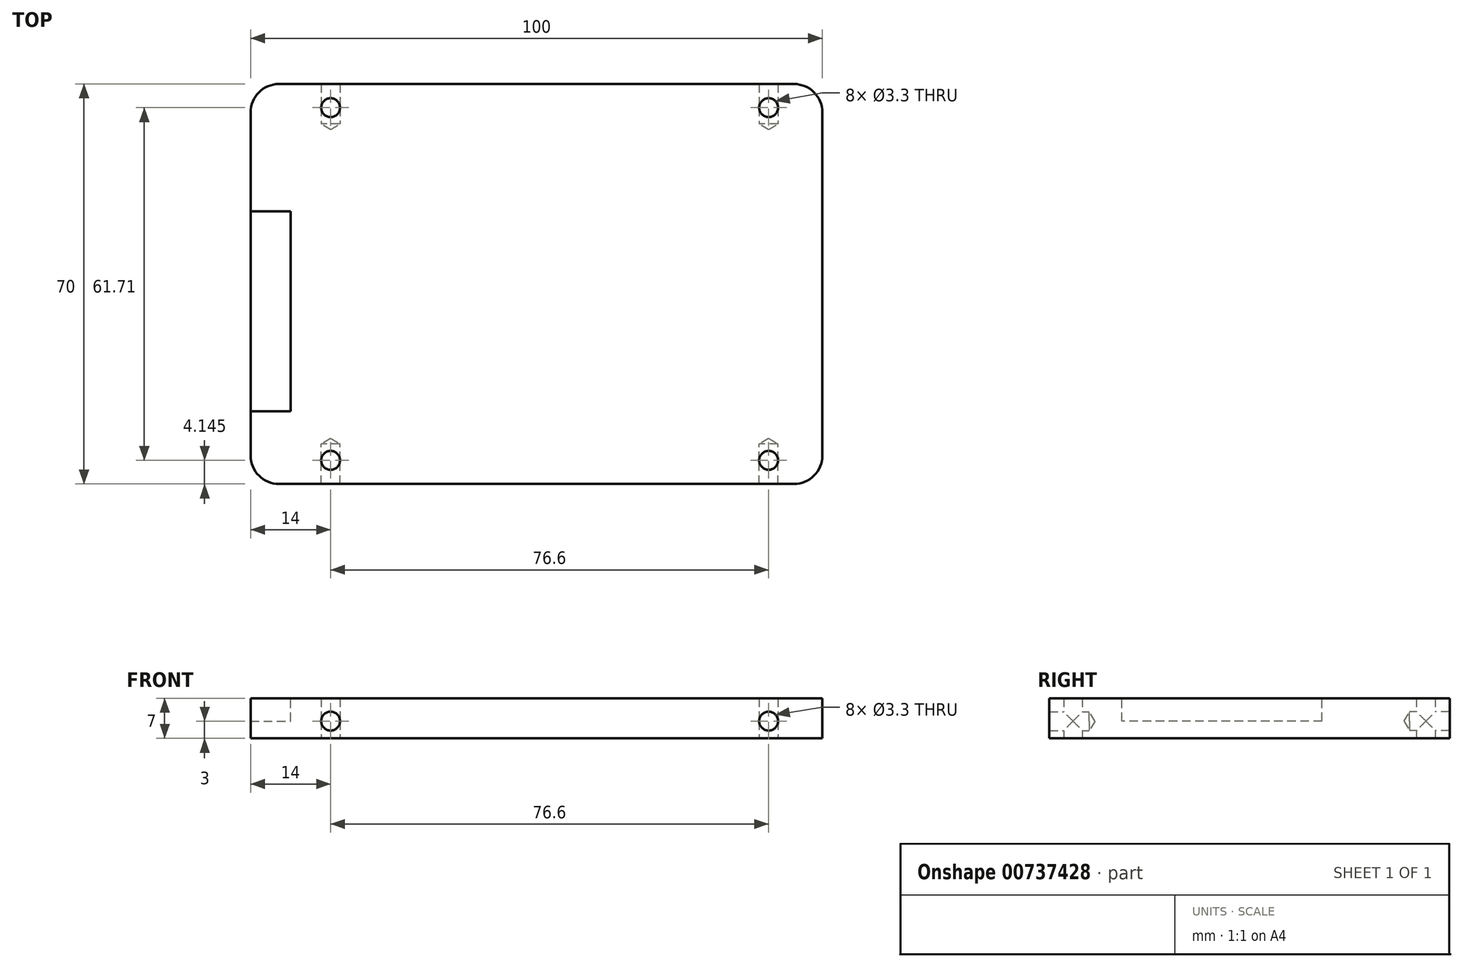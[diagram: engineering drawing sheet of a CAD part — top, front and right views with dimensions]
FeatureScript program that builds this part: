
annotation { "Feature Type Name" : "Feature", "Feature Type Description" : "" }
export const myFeature = defineFeature(function(context is Context, id is Id, definition is map)
    precondition{}
    {
        {
            var Q0;
            Q0=qCreatedBy(makeId("Top.planeOp"),FACE);
            var sketch = newSketch(context, id + "F0", { "sketchPlane" : qUnion([Q0])});
            skLineSegment(sketch, "E0.bottom", {"start": v(-50, 35) * mm, "end": v(50, 35) * mm});
            skLineSegment(sketch, "E0.top", {"start": v(-50, -35) * mm, "end": v(50, -35) * mm});
            skLineSegment(sketch, "E0.left", {"start": v(-50, 35) * mm, "end": v(-50, -35) * mm});
            skLineSegment(sketch, "E0.right", {"start": v(50, 35) * mm, "end": v(50, -35) * mm});
            skSolve(sketch);
        }
        {
            var Q0;
            Q0=makeQuery(id+"F0.imprint","IMPRINT",FACE,{"disambiguationData":[TD([[makeQuery(id+"F0.imprint","IMPRINT",EDGE,{"derivedFrom":sQuery(id+"F0.wireOp",EDGE,"E0.bottom")}),-1.0]])]});
            extrude(context, id + "F1", {"entities" : qUnion([Q0]), "depth" : 7 * mm});
        }
        {
            var Q0;
            Q0=makeQuery(id+"F1.opExtrude","SWEPT_EDGE",EDGE,{"disambiguationData":[OSD([sQuery(id+"F0.wireOp",EDGE,"E0.top"),sQuery(id+"F0.wireOp",EDGE,"E0.left")])]});
            var Q1;
            Q1=makeQuery(id+"F1.opExtrude","SWEPT_EDGE",EDGE,{"disambiguationData":[OSD([sQuery(id+"F0.wireOp",EDGE,"E0.top"),sQuery(id+"F0.wireOp",EDGE,"E0.right")])]});
            var Q2;
            Q2=makeQuery(id+"F1.opExtrude","SWEPT_EDGE",EDGE,{"disambiguationData":[OSD([sQuery(id+"F0.wireOp",EDGE,"E0.bottom"),sQuery(id+"F0.wireOp",EDGE,"E0.left")])]});
            var Q3;
            Q3=makeQuery(id+"F1.opExtrude","SWEPT_EDGE",EDGE,{"disambiguationData":[OSD([sQuery(id+"F0.wireOp",EDGE,"E0.bottom"),sQuery(id+"F0.wireOp",EDGE,"E0.right")])]});
            fillet(context, id + "F2", {"entities" : qUnion([Q0, Q1, Q2, Q3]), "radius" : 5 * mm, "tangentPropagation" : true, "allowEdgeOverflow" : false});
        }
        {
            var Q0;
            Q0=makeQuery(id+"F1.opExtrude","CAP_FACE",FACE,{"disambiguationData":[OSD([sQuery(id+"F0.wireOp",EDGE,"E0.bottom"),sQuery(id+"F0.wireOp",EDGE,"E0.top"),sQuery(id+"F0.wireOp",EDGE,"E0.left"),sQuery(id+"F0.wireOp",EDGE,"E0.right")])],"isStart":false});
            var sketch = newSketch(context, id + "F3", { "sketchPlane" : qUnion([Q0])});
            skPoint(sketch, "E1", {"position": v(-36, 30.86) * mm});
            skPoint(sketch, "E2", {"position": v(40.6, 30.86) * mm});
            skPoint(sketch, "E3", {"position": v(40.6, -30.86) * mm});
            skPoint(sketch, "E4", {"position": v(-36, -30.86) * mm});
            skSolve(sketch);
        }
        {
            var Q0;
            Q0=makeQuery(id+"F1.opExtrude","SWEPT_FACE",FACE,{"disambiguationData":[OSD([sQuery(id+"F0.wireOp",EDGE,"E0.top")])]});
            var sketch = newSketch(context, id + "F4", { "sketchPlane" : qUnion([Q0])});
            skPoint(sketch, "E5", {"position": v(-36, 3) * mm});
            skPoint(sketch, "E6", {"position": v(40.6, 3) * mm});
            skLineSegment(sketch, "E7", {"start": v(-36, 3) * mm, "end": v(-36, 7) * mm, "construction": true});
            skPoint(sketch, "E8.0", {"position": v(-36, 7) * mm});
            skPoint(sketch, "E9.0", {"position": v(40.6, 7) * mm});
            skLineSegment(sketch, "E10", {"start": v(40.6, 3) * mm, "end": v(40.6, 7) * mm, "construction": true});
            skLineSegment(sketch, "E11", {"start": v(-36, 3) * mm, "end": v(40.6, 3) * mm, "construction": true});
            skSolve(sketch);
        }
        {
            var Q0;
            Q0=makeQuery(id+"F1.opExtrude","SWEPT_FACE",FACE,{"disambiguationData":[OSD([sQuery(id+"F0.wireOp",EDGE,"E0.bottom")])]});
            var sketch = newSketch(context, id + "F5", { "sketchPlane" : qUnion([Q0])});
            skPoint(sketch, "E12.0", {"position": v(-40.6, 3) * mm});
            skPoint(sketch, "E12.1", {"position": v(36, 3) * mm});
            skSolve(sketch);
        }
        {
            var Q0;
            Q0=sQuery(id+"F3.wireOp",VERTEX,"E1");
            var Q1;
            Q1=sQuery(id+"F3.wireOp",VERTEX,"E4");
            var Q2;
            Q2=sQuery(id+"F3.wireOp",VERTEX,"E3");
            var Q3;
            Q3=sQuery(id+"F3.wireOp",VERTEX,"E2");
            var Q4;
            Q4=sQuery(id+"F5.wireOp",VERTEX,"E12.0");
            var Q5;
            Q5=sQuery(id+"F4.wireOp",VERTEX,"E5");
            var Q6;
            Q6=sQuery(id+"F4.wireOp",VERTEX,"E6");
            var Q7;
            Q7=sQuery(id+"F5.wireOp",VERTEX,"E12.1");
            var Q8;
            Q8=makeQuery(id+"F1.opExtrude","SWEPT_BODY",BODY,{"disambiguationData":[OSD([sQuery(id+"F0.wireOp",EDGE,"E0.bottom"),sQuery(id+"F0.wireOp",EDGE,"E0.top"),sQuery(id+"F0.wireOp",EDGE,"E0.left"),sQuery(id+"F0.wireOp",EDGE,"E0.right")])]});
            hole(context, id + "F6", {"style" : HoleStyle.SIMPLE, "endStyle" : HoleEndStyle.BLIND, "standardTappedOrClearance" : lookupTablePath({ "standard" : "ISO", "fit" : "Normal", "size" : "M3", "type" : "Clearance" }), "standardBlindInLast" : lookupTablePath({ "fit" : "Standard", "standard" : "ISO", "size" : "M3", "type" : "Clearance" }), "holeDiameter" : 3.3 * mm, "holeDepth" : 7 * mm, "tappedDepth" : 12 * mm, "tapClearance" : 3, "locations" : qUnion([Q0, Q1, Q2, Q3, Q4, Q5, Q6, Q7]), "scope" : qUnion([Q8])});
        }
        {
            var Q0;
            Q0=makeQuery(id+"F1.opExtrude","CAP_FACE",FACE,{"disambiguationData":[OSD([sQuery(id+"F0.wireOp",EDGE,"E0.bottom"),sQuery(id+"F0.wireOp",EDGE,"E0.top"),sQuery(id+"F0.wireOp",EDGE,"E0.left"),sQuery(id+"F0.wireOp",EDGE,"E0.right")])],"isStart":false});
            var sketch = newSketch(context, id + "F7", { "sketchPlane" : qUnion([Q0])});
            skLineSegment(sketch, "E13", {"start": v(-50, 12.7) * mm, "end": v(-43, 12.7) * mm});
            skLineSegment(sketch, "E14", {"start": v(-43, 12.7) * mm, "end": v(-43, -22.3) * mm});
            skLineSegment(sketch, "E15", {"start": v(-43, -22.3) * mm, "end": v(-50, -22.3) * mm});
            skLineSegment(sketch, "E16", {"start": v(-50, -22.3) * mm, "end": v(-50, 12.7) * mm});
            skLineSegment(sketch, "E17", {"start": v(-43, -4.8) * mm, "end": v(-50, -4.8) * mm, "construction": true});
            skSolve(sketch);
        }
        {
            var Q0;
            Q0=qSketchRegion(id+"F7",true);
            extrude(context, id + "F8", {"entities" : qUnion([Q0]), "operationType" : NewBodyOperationType.REMOVE, "oppositeDirection" : true, "depth" : 4 * mm});
        }
    });
